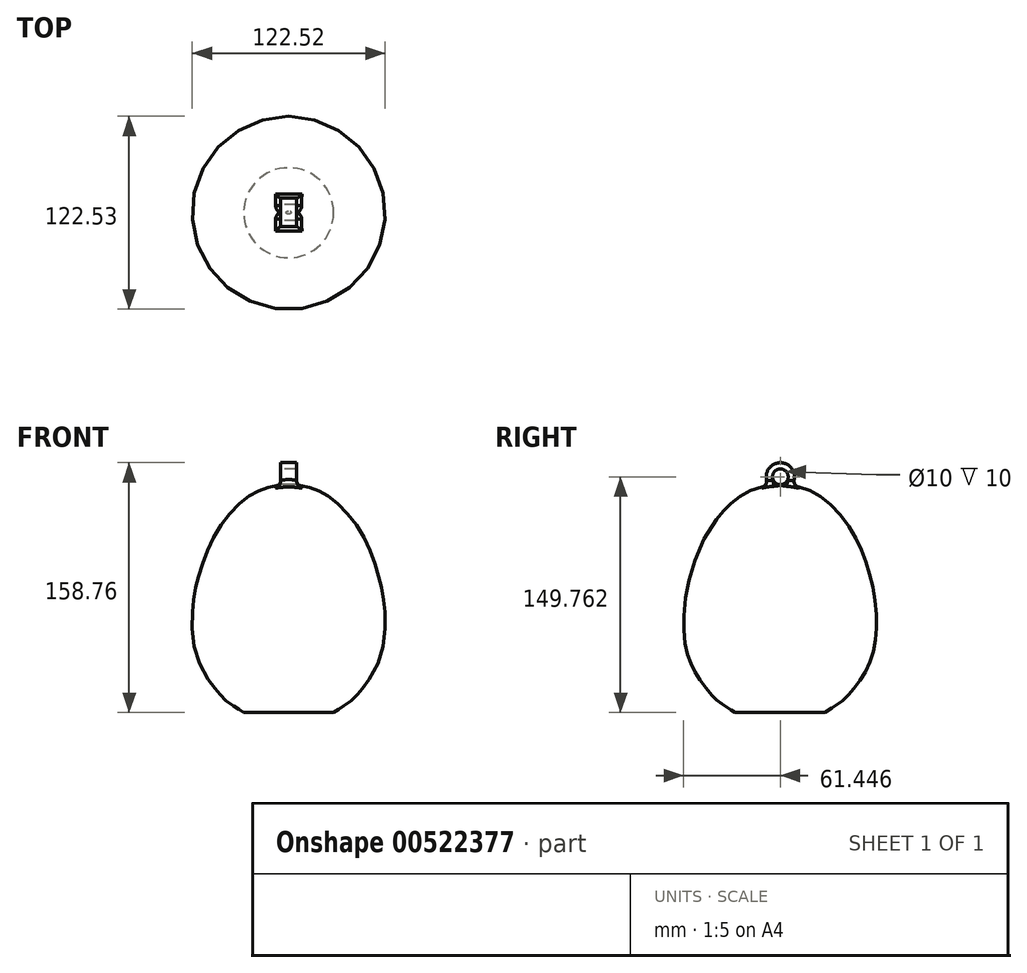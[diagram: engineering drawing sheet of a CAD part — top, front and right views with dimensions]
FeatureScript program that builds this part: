
annotation { "Feature Type Name" : "Feature", "Feature Type Description" : "" }
export const myFeature = defineFeature(function(context is Context, id is Id, definition is map)
    precondition{}
    {
        {
            var Q0;
            Q0=qCreatedBy(makeId("Right.planeOp"),FACE);
            var sketch = newSketch(context, id + "F0", { "sketchPlane" : qUnion([Q0])});
            skFitSpline(sketch, "E0", {"points": [v(-19.05, 70) * mm, v(-5.89, 68.07) * mm, v(6.83, 62.32) * mm, v(21.04, 48.3) * mm, v(31.03, 31.78) * mm, v(36.8, 16.41) * mm, v(41.02, -1.45) * mm, v(42.17, -21.23) * mm, v(40.44, -35.26) * mm, v(35.83, -47.36) * mm, v(30.07, -56.58) * mm, v(24.7, -63.3) * mm, v(19.12, -68.48) * mm, v(9.52, -74.82) * mm, v(9.71, -74.82) * mm], "startDerivative": vector(162.93, -0.84) * mm, "endDerivative": vector(32.7, 6.24) * mm});
            skLineSegment(sketch, "E1", {"start": v(9.52, -74.82) * mm, "end": v(-19.05, -74.82) * mm});
            skLineSegment(sketch, "E2", {"start": v(-19.05, -74.82) * mm, "end": v(-19.05, 70) * mm});
            skSolve(sketch);
        }
        {
            var Q0;
            {var subQ2=sQuery(id+"F0.wireOp",EDGE,"E1");Q0=makeQuery(id+"F0.imprint","IMPRINT",FACE,{"disambiguationData":[TD([[makeQuery(id+"F0.imprint","IMPRINT",EDGE,{"derivedFrom":subQ2}),-1.0]])]});}
            var Q1;
            {var subQ0=sQuery(id+"F0.wireOp",EDGE,"E2");var subQ1=sQuery(id+"F0.wireOp",EDGE,"E0");var subQ2=makeQuery(id+"F0.imprint","INTERSECT",VERTEX,{"derivedFrom":[subQ1,subQ0]});Q1=makeQuery(id+"F0.imprint","IMPRINT",FACE,{"disambiguationData":[TD([[makeQuery(id+"F0.imprint","IMPRINT",EDGE,{"disambiguationData":[TD([[subQ2,-1.0]])],"derivedFrom":subQ1}),-1.0]])]});}
            var Q2;
            Q2=sQuery(id+"F0.wireOp",EDGE,"E2");
            revolve(context, id + "F1", {"surfaceOperationType" : NewSurfaceOperationType.NEW, "entities" : qUnion([Q0, Q1]), "axis" : qUnion([Q2]), "revolveType" : RevolveType.FULL});
        }
        {
            var Q0;
            Q0=qCreatedBy(makeId("Right.planeOp"),FACE);
            var sketch = newSketch(context, id + "F2", { "sketchPlane" : qUnion([Q0])});
            skCircle(sketch, "E3", {"center": v(-18.87, 74.94) * mm, "radius": 5 * mm});
            skCircle(sketch, "E4", {"center": v(-18.87, 74.94) * mm, "radius": 9 * mm});
            skSolve(sketch);
        }
        {
            var Q0;
            Q0=makeQuery(id+"F2.imprint","IMPRINT",FACE,{"disambiguationData":[TD([[makeQuery(id+"F2.imprint","IMPRINT",EDGE,{"derivedFrom":sQuery(id+"F2.wireOp",EDGE,"E3")}),-1.0]])]});
            extrude(context, id + "F3", {"entities" : qUnion([Q0]), "operationType" : NewBodyOperationType.ADD, "depth" : 10 * mm, "offsetDistance" : 25 * mm, "symmetric" : true});
        }
        {
            var Q0;
            Q0=makeQuery(id+"F3.boolean.opBoolean","INTERSECT",EDGE,{"derivedFrom":[makeQuery(id+"F1.opRevolve","SWEPT_FACE",FACE,{"disambiguationData":[OSD([sQuery(id+"F0.wireOp",EDGE,"E0")])]}),makeQuery(id+"F3.opExtrude","CAP_FACE",FACE,{"disambiguationData":[OSD([sQuery(id+"F2.wireOp",EDGE,"E3"),sQuery(id+"F2.wireOp",EDGE,"E4")])],"isStart":true})]});
            var Q1;
            Q1=makeQuery(id+"F3.boolean.opBoolean","INTERSECT",EDGE,{"derivedFrom":[makeQuery(id+"F1.opRevolve","SWEPT_FACE",FACE,{"disambiguationData":[OSD([sQuery(id+"F0.wireOp",EDGE,"E0")])]}),makeQuery(id+"F3.opExtrude","CAP_FACE",FACE,{"disambiguationData":[OSD([sQuery(id+"F2.wireOp",EDGE,"E3"),sQuery(id+"F2.wireOp",EDGE,"E4")])],"isStart":false})]});
            var Q2;
            Q2=makeQuery(id+"F3.boolean.opBoolean","INTERSECT",EDGE,{"disambiguationData":[OD(1.0)],"derivedFrom":[makeQuery(id+"F1.opRevolve","SWEPT_FACE",FACE,{"disambiguationData":[OSD([sQuery(id+"F0.wireOp",EDGE,"E0")])]}),makeQuery(id+"F3.opExtrude","SWEPT_FACE",FACE,{"disambiguationData":[OSD([sQuery(id+"F2.wireOp",EDGE,"E4")])]})]});
            var Q3;
            Q3=makeQuery(id+"F3.boolean.opBoolean","INTERSECT",EDGE,{"disambiguationData":[OD(0.0)],"derivedFrom":[makeQuery(id+"F1.opRevolve","SWEPT_FACE",FACE,{"disambiguationData":[OSD([sQuery(id+"F0.wireOp",EDGE,"E0")])]}),makeQuery(id+"F3.opExtrude","SWEPT_FACE",FACE,{"disambiguationData":[OSD([sQuery(id+"F2.wireOp",EDGE,"E4")])]})]});
            fillet(context, id + "F4", {"entities" : qUnion([Q0, Q1, Q2, Q3]), "radius" : 4 * mm, "tangentPropagation" : true, "allowEdgeOverflow" : false});
        }
        {
            var Q0;
            Q0=qCreatedBy(makeId("Front.planeOp"),FACE);
            cPlane(context, id + "F5", {"entities" : qUnion([Q0]), "cplaneType" : CPlaneType.OFFSET, "offset" : 50 * mm, "oppositeDirection" : true, "width" : 150 * mm, "height" : 150 * mm});
        }
    });
